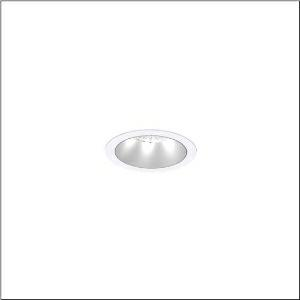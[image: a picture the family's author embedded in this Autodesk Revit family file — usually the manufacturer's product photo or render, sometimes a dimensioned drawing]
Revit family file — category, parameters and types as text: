
# Revit family: lunis_21_m_51db19mc91c
name_source: partatom
category: Lighting Fixtures
units: mm (PartAtom-declared; Revit-internal decimal feet)

## family parameters
Cut with Voids When Loaded = No
Host = Face
Light Source = No
Part Type = Normal
Room Calculation Point = No
Round Connector Dimension = Use Diameter
Shared = No

## types (1)
- --- (1 x LED, 3840 lm, 25.5 W, 6500K)
    Apparent Load = 26 VA
    CIE Flux Codes = 93 99 100 100 100
    Color Rendering = 80
    Color Temperature = 6500K
    Default Elevation = 1800 mm
    Description = Lunis 21,  M, downlight, light control with lens, of PMMA, anti glare with reflector, of PC, matt, light emission: direct distribution, LED rated luminous flux: 1.770lm, light colour: 830/840/865, with terminal, 3-pole, mains connection: 220..240V, AC/DC, 0/50..60Hz, housing, round, of diecast aluminium, traffic white (RAL 9016), diameter: 115mm, clamping range: 1..40mm, protection rating (complete): IP20, protection rating (on room side): IP54, insulation class (complete): insulation class II (safety insulation), certification: CE, impact resistance: IK03, packaging unit: 1 piece
    Height = 0 mm  [stored 0 ft]
    Lamp = 1 x LED
    Lamp Light Flux = 3840 lm
    Lamp Power = 25.5 W
    Lamp count = 1
    Length = 115 mm
    Luminous efficacy = 151 lm/W
    Manufacturer = Siteco
    ModVariant = No
    Model = 51DB19MC91C
    Mounting Place = Ceiling
    Mounting Type = Recessed
    Number of Poles = 1
    OnlyDefault = Yes
    Power Factor = 1
    Product Name = Lunis 21 M
    Product group = downlight
    ProductGroupID = 400
    Protection Class = Protection class II
    Protection Degree = IP 20
    RLX_Detail_Level = 1
    RLX_Emergency_Light_Flux = 0 lm
    RLX_Emergency_Type = 0
    RLX_Emergency_Type_DB = No
    RlxData = <blob elided: 15021 chars, md5=03591d74>
    Socket = socket
    Standby Power = 0 W
    System Light Flux = 3840 lm
    System Power = 26 W
    Type Comments = individual setting: colour temperature 6500K, luminous flux: 100 % | (ON | ON | OFF | OFF) | 700 mA
    Type Image = l_1290856.jpg
    URL = http://relux.com
    VarID = @adj_019100
    Voltage = 0 V
    Weight = 0.00 kg
    Width = 0 mm  [stored 0 ft]

note: [stored X ft] marks values corroborated as IEEE doubles in the binary element streams (Revit-internal decimal feet)

## geometry (parser evidence)
native form markers: Sweep x11
no freeform markers — native parametric forms only
